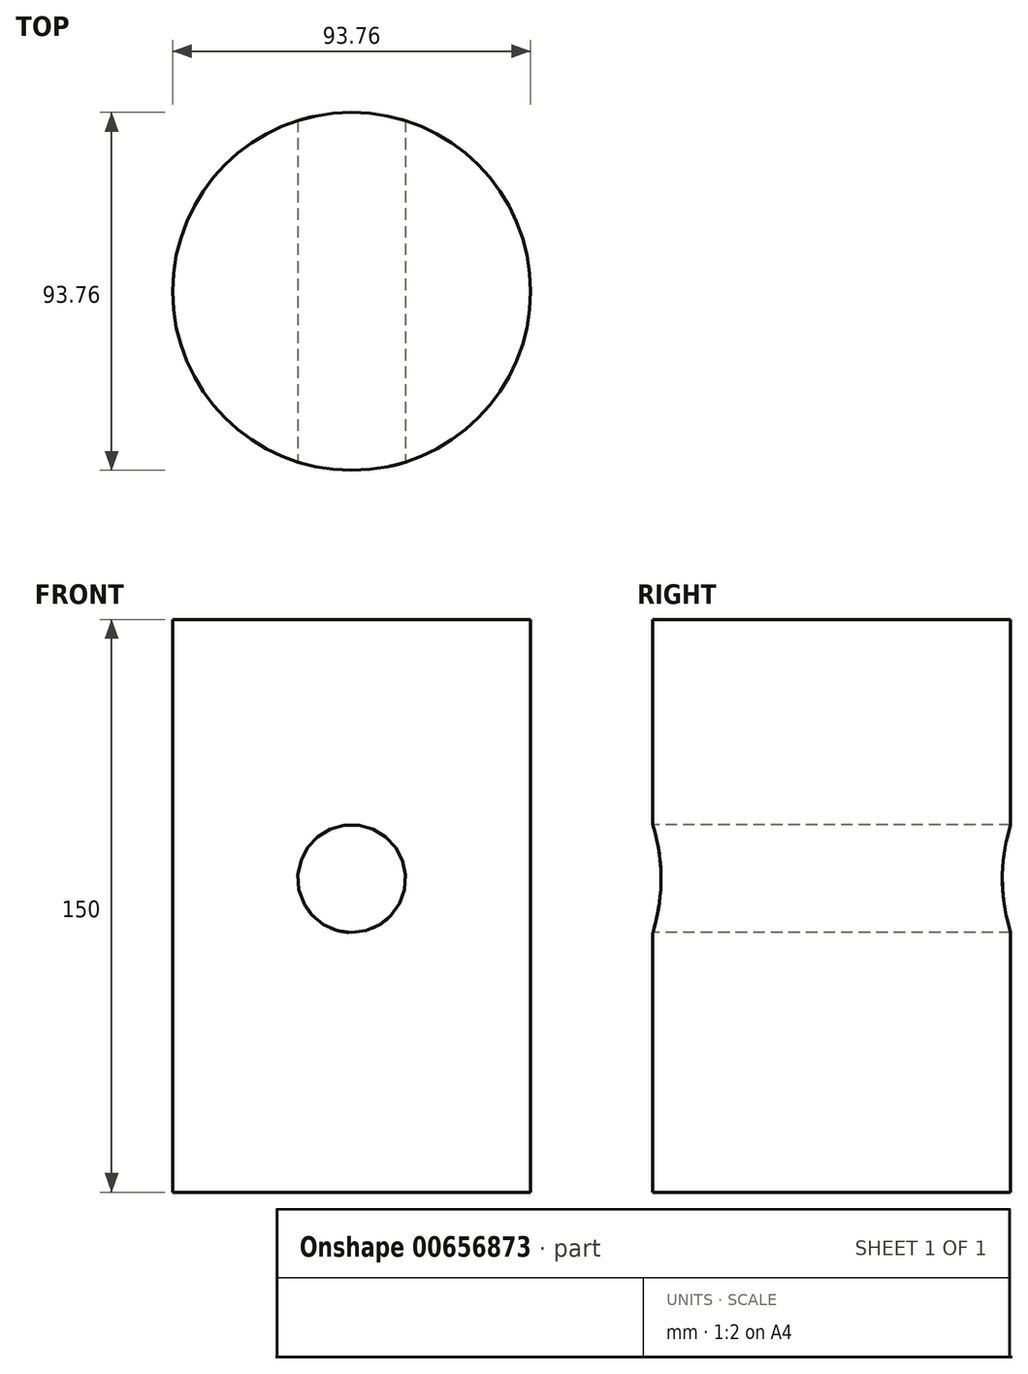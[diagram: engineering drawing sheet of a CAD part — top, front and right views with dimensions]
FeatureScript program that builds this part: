
annotation { "Feature Type Name" : "Feature", "Feature Type Description" : "" }
export const myFeature = defineFeature(function(context is Context, id is Id, definition is map)
    precondition{}
    {
        {
            var Q0;
            Q0=qCreatedBy(makeId("Top.planeOp"),FACE);
            var sketch = newSketch(context, id + "F0", { "sketchPlane" : qUnion([Q0])});
            skCircle(sketch, "E0", {"center": v(0, 0) * mm, "radius": 46.88 * mm});
            skSolve(sketch);
        }
        {
            var Q0;
            Q0 = qSketchRegion(id + "F0", true);
            extrude(context, id + "F1", {"entities" : qUnion([Q0]), "depth" : 150 * mm, "offsetDistance" : 25 * mm});
        }
        {
            var Q0;
            Q0=qCreatedBy(makeId("Front.planeOp"),FACE);
            cPlane(context, id + "F2", {"entities" : qUnion([Q0]), "cplaneType" : CPlaneType.OFFSET, "offset" : 50 * mm, "width" : 150 * mm, "height" : 150 * mm});
        }
        {
            var Q0;
            Q0=qCreatedBy(id+"F2.planeOp",FACE);
            var sketch = newSketch(context, id + "F3", { "sketchPlane" : qUnion([Q0])});
            skCircle(sketch, "E1", {"center": v(0, 82.13) * mm, "radius": 14.1 * mm});
            skSolve(sketch);
        }
        {
            var Q0;
            Q0=makeQuery(id+"F3.imprint","IMPRINT",FACE,{"disambiguationData":[TD([[makeQuery(id+"F3.imprint","IMPRINT",EDGE,{"derivedFrom":sQuery(id+"F3.wireOp",EDGE,"E1")}),1.0]])]});
            extrude(context, id + "F4", {"entities" : qUnion([Q0]), "operationType" : NewBodyOperationType.REMOVE, "oppositeDirection" : true, "depth" : 100 * mm, "offsetDistance" : 25 * mm});
        }
    });
